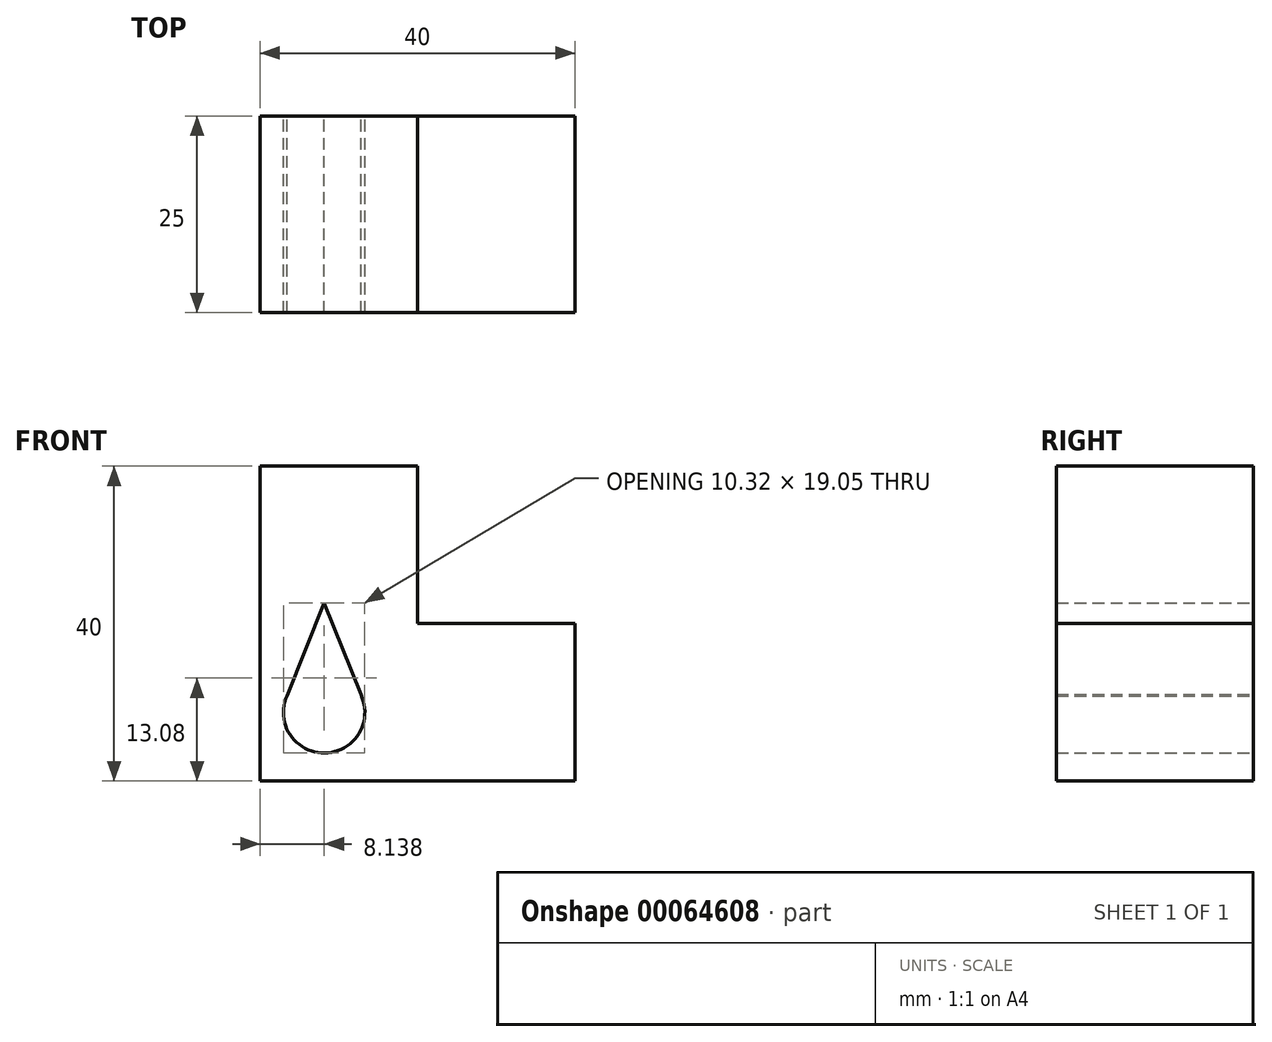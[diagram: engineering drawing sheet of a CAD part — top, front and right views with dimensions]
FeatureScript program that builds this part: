
annotation { "Feature Type Name" : "Feature", "Feature Type Description" : "" }
export const myFeature = defineFeature(function(context is Context, id is Id, definition is map)
    precondition{}
    {
        {
            var Q0;
            Q0=qCreatedBy(makeId("Front.planeOp"),FACE);
            var sketch = newSketch(context, id + "F0", { "sketchPlane" : qUnion([Q0])});
            skLineSegment(sketch, "E0.bottom", {"start": v(0, 0) * mm, "end": v(0, 0) * mm});
            skLineSegment(sketch, "E0.top", {"start": v(0, 4.87) * mm, "end": v(0, 4.87) * mm});
            skLineSegment(sketch, "E0.left", {"start": v(0, 0) * mm, "end": v(0, 4.87) * mm});
            skLineSegment(sketch, "E0.right", {"start": v(0, 0) * mm, "end": v(0, 4.87) * mm});
            skLineSegment(sketch, "E1.bottom", {"start": v(0, 0) * mm, "end": v(20, 0) * mm});
            skLineSegment(sketch, "E1.top", {"start": v(0, 40) * mm, "end": v(20, 40) * mm});
            skLineSegment(sketch, "E1.left", {"start": v(0, 0) * mm, "end": v(0, 40) * mm});
            skLineSegment(sketch, "E1.right", {"start": v(20, 0) * mm, "end": v(20, 40) * mm});
            skLineSegment(sketch, "E2.bottom", {"start": v(20, 0) * mm, "end": v(40, 0) * mm});
            skLineSegment(sketch, "E2.top", {"start": v(20, 20) * mm, "end": v(40, 20) * mm});
            skLineSegment(sketch, "E2.left", {"start": v(20, 0) * mm, "end": v(20, 20) * mm});
            skLineSegment(sketch, "E2.right", {"start": v(40, 0) * mm, "end": v(40, 20) * mm});
            skArc(sketch, "E3", {"start": v(3.4, 10.83) * mm, "mid": v(8.2, 3.56) * mm, "end": v(12.8, 10.97) * mm});
            skLineSegment(sketch, "E4", {"start": v(3.26, 10.48) * mm, "end": v(8.13, 22.6) * mm});
            skLineSegment(sketch, "E5", {"start": v(12.8, 10.97) * mm, "end": v(8.13, 22.6) * mm});
            skSolve(sketch);
        }
        {
            var Q0;
            Q0 = qSketchRegion(id + "F0", true);
            extrude(context, id + "F1", {"entities" : qUnion([Q0]), "depth" : 25 * mm});
        }
    });
